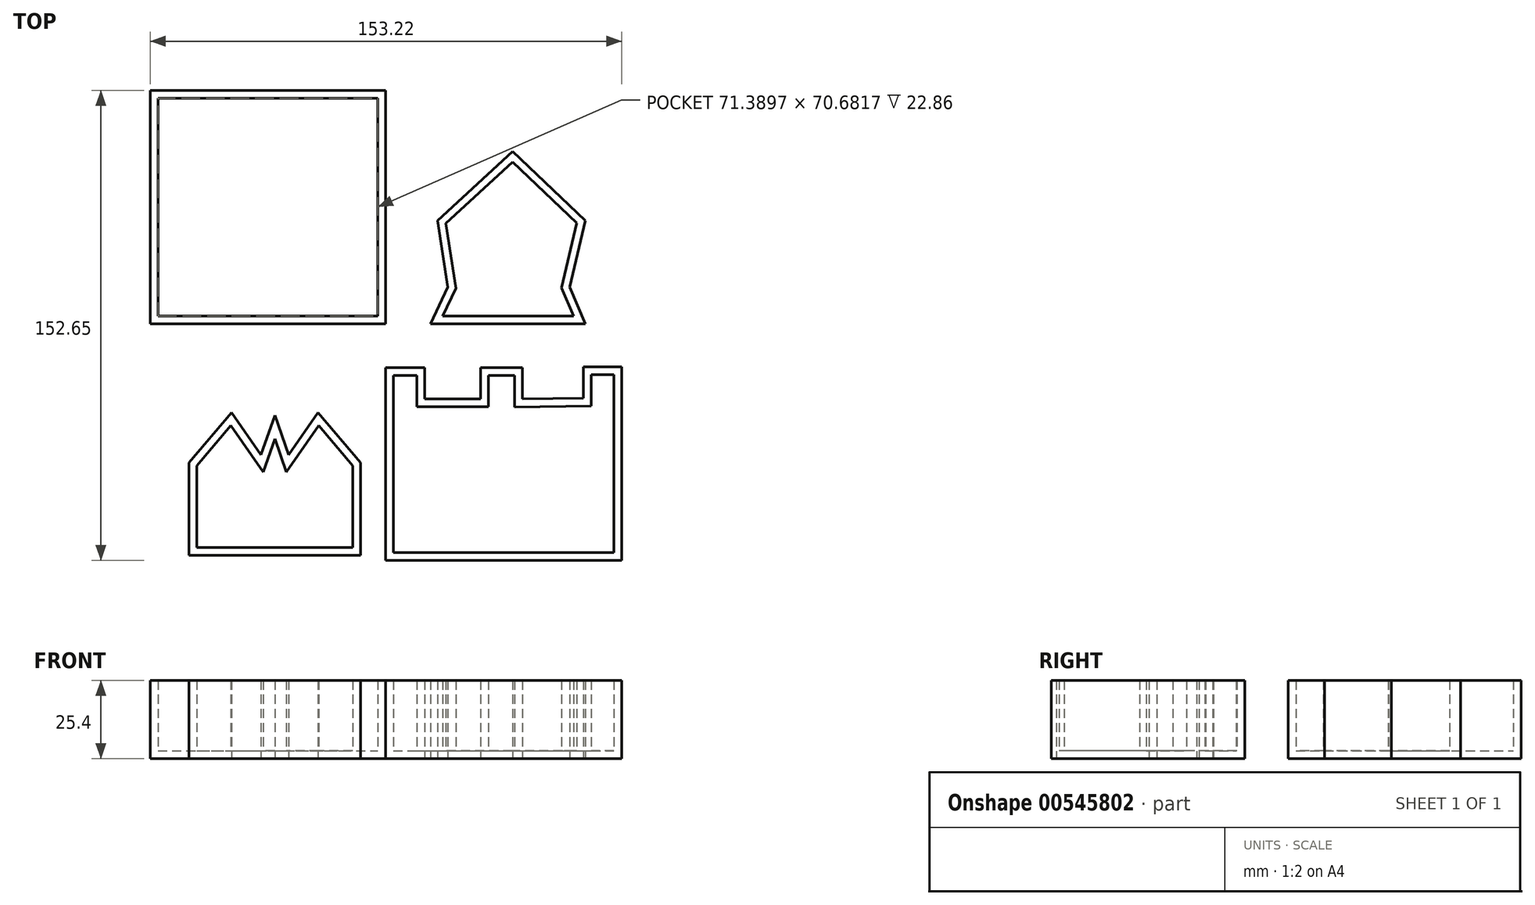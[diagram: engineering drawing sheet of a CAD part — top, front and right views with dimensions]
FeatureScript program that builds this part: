
annotation { "Feature Type Name" : "Feature", "Feature Type Description" : "" }
export const myFeature = defineFeature(function(context is Context, id is Id, definition is map)
    precondition{}
    {
        {
            var Q0;
            Q0=qCreatedBy(makeId("Top.planeOp"),FACE);
            var sketch = newSketch(context, id + "F0", { "sketchPlane" : qUnion([Q0])});
            skLineSegment(sketch, "E0", {"start": v(0, 0) * mm, "end": v(0, 75.76) * mm});
            skLineSegment(sketch, "E1", {"start": v(0, 75.76) * mm, "end": v(-76.47, 75.76) * mm});
            skLineSegment(sketch, "E2", {"start": v(-76.47, 75.76) * mm, "end": v(-76.47, 0) * mm});
            skLineSegment(sketch, "E3", {"start": v(-76.47, 0) * mm, "end": v(0, 0) * mm});
            skSolve(sketch);
        }
        {
            var Q0;
            Q0=makeQuery(id+"F0.imprint","IMPRINT",FACE,{"disambiguationData":[TD([[makeQuery(id+"F0.imprint","IMPRINT",EDGE,{"derivedFrom":sQuery(id+"F0.wireOp",EDGE,"E0")}),1.0]])]});
            extrude(context, id + "F1", {"entities" : qUnion([Q0]), "depth" : 25.4 * mm, "offsetDistance" : 25.4 * mm});
        }
        {
            var Q0;
            Q0=makeQuery(id+"F1.opExtrude","CAP_FACE",FACE,{"disambiguationData":[OSD([sQuery(id+"F0.wireOp",EDGE,"E0"),sQuery(id+"F0.wireOp",EDGE,"E1"),sQuery(id+"F0.wireOp",EDGE,"E2"),sQuery(id+"F0.wireOp",EDGE,"E3")])],"isStart":false});
            shell(context, id + "F2", {"entities" : qUnion([Q0]), "thickness" : 2.54 * mm});
        }
        {
            var Q0;
            Q0=qCreatedBy(makeId("Top.planeOp"),FACE);
            var sketch = newSketch(context, id + "F3", { "sketchPlane" : qUnion([Q0])});
            skLineSegment(sketch, "E4", {"start": v(0, -76.9) * mm, "end": v(75.34, -76.9) * mm});
            skLineSegment(sketch, "E5", {"start": v(76.75, -26.2) * mm, "end": v(76.75, -14.02) * mm});
            skLineSegment(sketch, "E6", {"start": v(76.75, -14.02) * mm, "end": v(64.3, -14.02) * mm});
            skLineSegment(sketch, "E7", {"start": v(64.3, -14.02) * mm, "end": v(64.3, -24.22) * mm});
            skLineSegment(sketch, "E8", {"start": v(0, -14.3) * mm, "end": v(12.74, -14.3) * mm});
            skLineSegment(sketch, "E9", {"start": v(12.74, -14.3) * mm, "end": v(12.74, -24.5) * mm});
            skLineSegment(sketch, "E10", {"start": v(0, -14.3) * mm, "end": v(0, -27.33) * mm});
            skLineSegment(sketch, "E11", {"start": v(0, -27.33) * mm, "end": v(0, -76.9) * mm});
            skLineSegment(sketch, "E12", {"start": v(76.75, -26.2) * mm, "end": v(76.75, -76.9) * mm});
            skLineSegment(sketch, "E13", {"start": v(76.75, -76.9) * mm, "end": v(75.34, -76.9) * mm});
            skLineSegment(sketch, "E14", {"start": v(12.74, -24.5) * mm, "end": v(30.87, -24.5) * mm});
            skLineSegment(sketch, "E15", {"start": v(30.87, -24.5) * mm, "end": v(30.87, -14.3) * mm});
            skLineSegment(sketch, "E16", {"start": v(30.87, -14.3) * mm, "end": v(44.47, -14.3) * mm});
            skLineSegment(sketch, "E17", {"start": v(44.47, -14.3) * mm, "end": v(44.47, -24.5) * mm});
            skLineSegment(sketch, "E18", {"start": v(44.47, -24.5) * mm, "end": v(64.3, -24.22) * mm});
            skSolve(sketch);
        }
        {
            var Q0;
            Q0=makeQuery(id+"F3.imprint","IMPRINT",FACE,{"disambiguationData":[TD([[makeQuery(id+"F3.imprint","IMPRINT",EDGE,{"derivedFrom":sQuery(id+"F3.wireOp",EDGE,"E4")}),1.0]])]});
            extrude(context, id + "F4", {"entities" : qUnion([Q0]), "depth" : 25.4 * mm, "offsetDistance" : 25.4 * mm});
        }
        {
            var Q0;
            Q0=makeQuery(id+"F4.opExtrude","CAP_FACE",FACE,{"disambiguationData":[OSD([sQuery(id+"F3.wireOp",EDGE,"E4"),sQuery(id+"F3.wireOp",EDGE,"E5"),sQuery(id+"F3.wireOp",EDGE,"E6"),sQuery(id+"F3.wireOp",EDGE,"E7"),sQuery(id+"F3.wireOp",EDGE,"E8"),sQuery(id+"F3.wireOp",EDGE,"E9"),sQuery(id+"F3.wireOp",EDGE,"E10"),sQuery(id+"F3.wireOp",EDGE,"E11"),sQuery(id+"F3.wireOp",EDGE,"E12"),sQuery(id+"F3.wireOp",EDGE,"E13"),sQuery(id+"F3.wireOp",EDGE,"E14"),sQuery(id+"F3.wireOp",EDGE,"E15"),sQuery(id+"F3.wireOp",EDGE,"E16"),sQuery(id+"F3.wireOp",EDGE,"E17"),sQuery(id+"F3.wireOp",EDGE,"E18")])],"isStart":false});
            shell(context, id + "F5", {"entities" : qUnion([Q0]), "thickness" : 2.54 * mm});
        }
        {
            var Q0;
            Q0=qCreatedBy(makeId("Top.planeOp"),FACE);
            var sketch = newSketch(context, id + "F6", { "sketchPlane" : qUnion([Q0])});
            skLineSegment(sketch, "E19", {"start": v(-66.04, -75.24) * mm, "end": v(-35.97, -75.24) * mm});
            skLineSegment(sketch, "E20", {"start": v(-63.8, -45.17) * mm, "end": v(-63.8, -75.24) * mm});
            skLineSegment(sketch, "E21", {"start": v(-63.8, -45.17) * mm, "end": v(-50.02, -28.87) * mm});
            skLineSegment(sketch, "E22", {"start": v(-50.02, -28.87) * mm, "end": v(-40.47, -42.64) * mm});
            skLineSegment(sketch, "E23", {"start": v(-35.97, -29.71) * mm, "end": v(-40.47, -42.64) * mm});
            skLineSegment(sketch, "E24.MirrorCS", {"start": v(-8.15, -45.17) * mm, "end": v(-8.15, -75.24) * mm});
            skLineSegment(sketch, "E25.MirrorCS", {"start": v(-8.15, -45.17) * mm, "end": v(-21.92, -28.87) * mm});
            skLineSegment(sketch, "E26.MirrorCS", {"start": v(-21.92, -28.87) * mm, "end": v(-31.47, -42.64) * mm});
            skLineSegment(sketch, "E27.MirrorCS", {"start": v(-35.97, -29.71) * mm, "end": v(-31.47, -42.64) * mm});
            skLineSegment(sketch, "E28.MirrorCS", {"start": v(-5.9, -75.24) * mm, "end": v(-35.97, -75.24) * mm});
            skSolve(sketch);
        }
        {
            var Q0;
            {var subQ0=sQuery(id+"F6.wireOp",EDGE,"E20");Q0=makeQuery(id+"F6.imprint","IMPRINT",FACE,{"disambiguationData":[TD([[makeQuery(id+"F6.imprint","IMPRINT",EDGE,{"derivedFrom":subQ0}),1.0]])]});}
            extrude(context, id + "F7", {"entities" : qUnion([Q0]), "depth" : 25.4 * mm, "offsetDistance" : 25.4 * mm});
        }
        {
            var Q0;
            Q0=makeQuery(id+"F7.opExtrude","CAP_FACE",FACE,{"disambiguationData":[OSD([sQuery(id+"F6.wireOp",EDGE,"E19"),sQuery(id+"F6.wireOp",EDGE,"E20"),sQuery(id+"F6.wireOp",EDGE,"E21"),sQuery(id+"F6.wireOp",EDGE,"E22"),sQuery(id+"F6.wireOp",EDGE,"E23"),sQuery(id+"F6.wireOp",EDGE,"E24.MirrorCS"),sQuery(id+"F6.wireOp",EDGE,"E25.MirrorCS"),sQuery(id+"F6.wireOp",EDGE,"E26.MirrorCS"),sQuery(id+"F6.wireOp",EDGE,"E27.MirrorCS"),sQuery(id+"F6.wireOp",EDGE,"E28.MirrorCS")])],"isStart":false});
            shell(context, id + "F8", {"entities" : qUnion([Q0]), "thickness" : 2.54 * mm});
        }
        {
            var Q0;
            Q0=qCreatedBy(makeId("Top.planeOp"),FACE);
            var sketch = newSketch(context, id + "F9", { "sketchPlane" : qUnion([Q0])});
            skLineSegment(sketch, "E29", {"start": v(14.61, 0) * mm, "end": v(64.92, 0) * mm});
            skLineSegment(sketch, "E30", {"start": v(64.92, 0) * mm, "end": v(59.86, 11.88) * mm});
            skLineSegment(sketch, "E31", {"start": v(59.86, 11.88) * mm, "end": v(64.92, 33.52) * mm});
            skLineSegment(sketch, "E32", {"start": v(64.92, 33.52) * mm, "end": v(41.31, 56) * mm});
            skLineSegment(sketch, "E33", {"start": v(41.31, 56) * mm, "end": v(16.86, 33.52) * mm});
            skLineSegment(sketch, "E34", {"start": v(16.86, 33.52) * mm, "end": v(20.24, 11.88) * mm});
            skLineSegment(sketch, "E35", {"start": v(20.24, 11.88) * mm, "end": v(14.61, 0) * mm});
            skSolve(sketch);
        }
        {
            var Q0;
            Q0 = qSketchRegion(id + "F9", true);
            extrude(context, id + "F10", {"entities" : qUnion([Q0]), "depth" : 25.4 * mm, "offsetDistance" : 25.4 * mm});
        }
        {
            var Q0;
            Q0=makeQuery(id+"F10.opExtrude","CAP_FACE",FACE,{"disambiguationData":[OSD([sQuery(id+"F9.wireOp",EDGE,"E29"),sQuery(id+"F9.wireOp",EDGE,"E30"),sQuery(id+"F9.wireOp",EDGE,"E31"),sQuery(id+"F9.wireOp",EDGE,"E32"),sQuery(id+"F9.wireOp",EDGE,"E33"),sQuery(id+"F9.wireOp",EDGE,"E34"),sQuery(id+"F9.wireOp",EDGE,"E35")])],"isStart":false});
            shell(context, id + "F11", {"entities" : qUnion([Q0]), "thickness" : 2.54 * mm});
        }
    });
